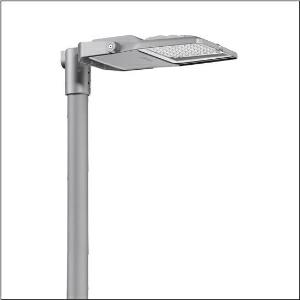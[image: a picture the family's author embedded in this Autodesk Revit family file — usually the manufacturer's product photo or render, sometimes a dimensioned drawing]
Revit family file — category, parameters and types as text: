
# Revit family: floodlight_fl_21_iq_mini___pl64_5xa7771b2e3a_ab64
name_source: partatom
category: Lighting Fixtures
units: mm (PartAtom-declared; Revit-internal decimal feet)

## family parameters
Cut with Voids When Loaded = No
Host = Face
Light Source = No
Part Type = Normal
Room Calculation Point = No
Round Connector Dimension = Use Diameter
Shared = No

## types (1)
- --- (1 x LED, 6020 lm, 45.5 W, 3000K)
    Apparent Load = 46 VA
    CIE Flux Codes = 28 80 98 100 100
    Color Rendering = 70
    Color Temperature = 3000K
    Default Elevation = 1800 mm
    Description = Floodlight FL 21 iQ mini, floodlight, primary light control with lens, of PMMA, primary optical cover: protective disc, of toughened safety glass, transparent, light distribution: PL64, light emission: direct distribution, installation type: surface-mounted, LED, High Power LED, rated luminous flux: 6.020lm, luminous efficacy: 132lm/W, light colour: 730, colour temperature: 3000K, control: Auto-Match, Temp-Guard, Lumen-Switch, Night-Set, Smart-Wire, Light-Fading, Desk-Remote (wireless, voltage-free reading and setting of iQ features in the workshop via application-optimized NFC function/RFID function), optimised constant luminous flux control (CLO 2.0), with terminal, 6-pole, mains connection: 220..240V, AC, 50/60Hz, start of lifetime: 46W, end of service life: 48W, reduction: 22W, luminaire housing, of diecast aluminium, powder-coated, Siteco® metallic grey (DB 702S), corrosivity category C5 mid according to DIN EN ISO 12944, sealing non-destructively replaceable, please order mast flange separately, mast bracket, of steel, galvanised, powder-coated, Siteco® metallic grey (DB 702S), protection rating (complete): IP66, insulation class (complete): insulation class II (safety insulation), certification: CE, ENEC, VDE, protection symbol: D, impact resistance: IK08, permissible operating ambient temperature: -40..+40°C, permissible operating ambient temperature for outdoor applications: -40..+50°C, standard: DIN EN 12944, LABS conformity tested according to VDMA 24364:2018-05, packaging unit: 1 piece

Light Distribution: PL64
    Height = 70 mm
    Lamp = 1 x LED
    Lamp Light Flux = 6020 lm
    Lamp Power = 45.5 W
    Lamp count = 1
    Length = 485 mm
    Luminous efficacy = 132 lm/W
    Manufacturer = Siteco
    ModVariant = No
    Model = 5XA7771B2E3A
    Number of Poles = 1
    OnlyDefault = Yes
    Power Factor = 1
    Product Name = Floodlight FL 21 iQ mini | PL64
    Product group = floodlight | pylon annexe
    ProductGroupID = 6200
    Protection Class = Protection class II
    Protection Degree = IP 66
    RLX_Detail_Level = 1
    RLX_Emergency_Light_Flux = 0 lm
    RLX_Emergency_Type = 0
    RLX_Emergency_Type_DB = No
    RlxData = <blob elided: 101205 chars, md5=eab4b31f>
    Socket = socket
    Standby Power = 0 W
    System Light Flux = 6020 lm
    System Power = 46 W
    Type Comments = factory setting: luminous flux: 100 % | dim-lin: 254 | 463 mA
    Type Image = l_1007125.jpg
    URL = http://relux.com
    VarID = @adj_117305
    Voltage = 0 V
    Weight = 0.00 kg
    Width = 337 mm

## geometry (parser evidence)
native form markers: Blend x4, Sweep x12
no freeform markers — native parametric forms only
